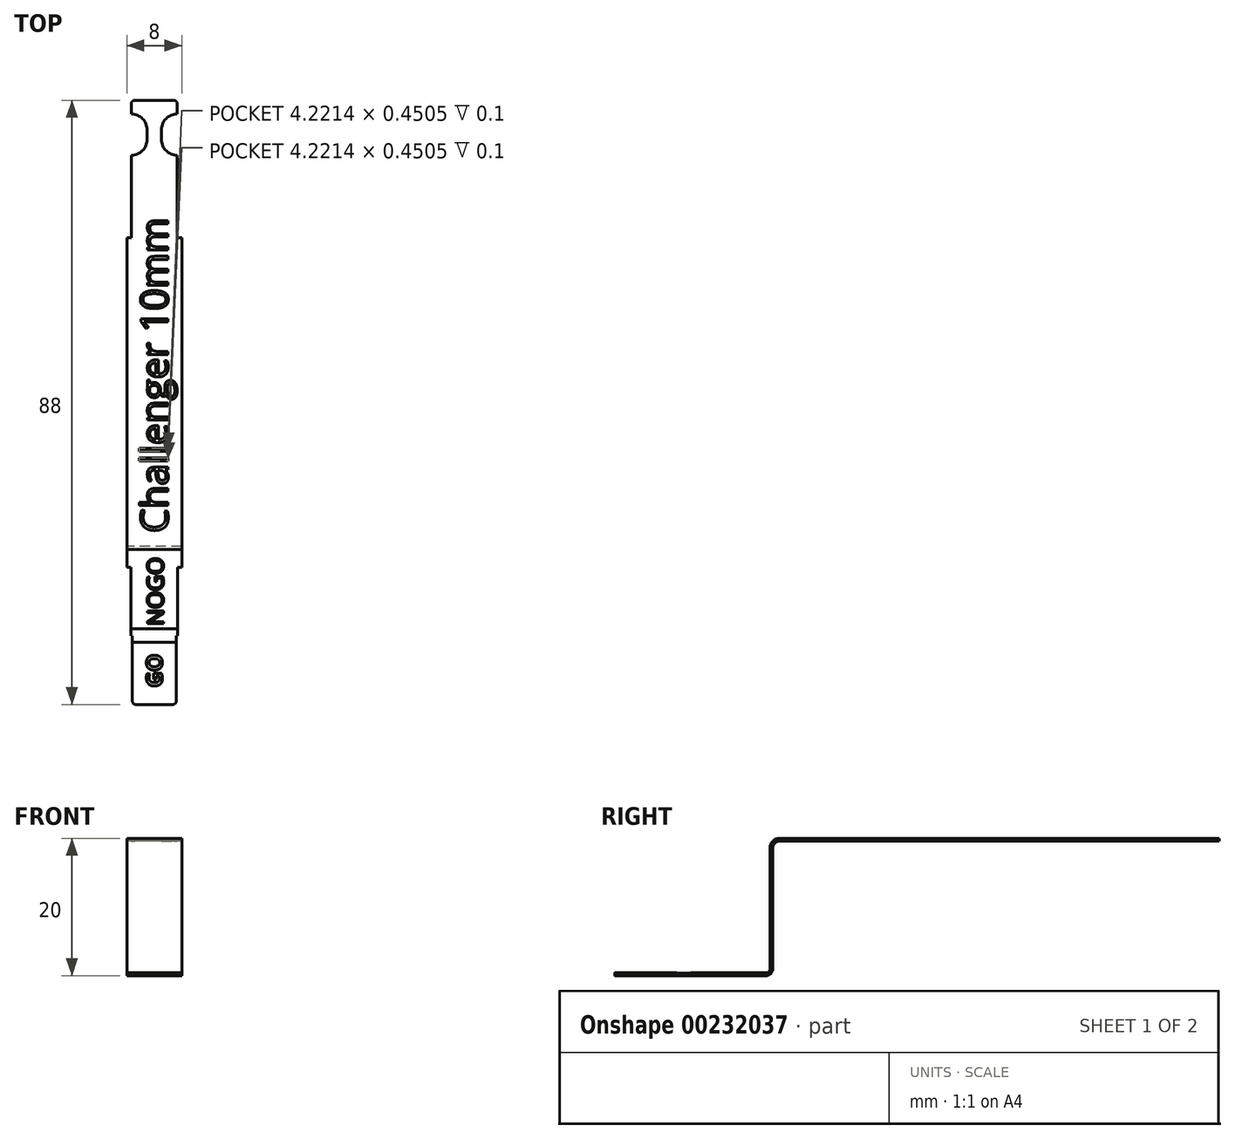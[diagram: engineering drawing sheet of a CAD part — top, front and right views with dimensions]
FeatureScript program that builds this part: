
annotation { "Feature Type Name" : "Feature", "Feature Type Description" : "" }
export const myFeature = defineFeature(function(context is Context, id is Id, definition is map)
    precondition{}
    {
        {
            var Q0;
            Q0=qCreatedBy(makeId("Front.planeOp"),FACE);
            var sketch = newSketch(context, id + "F0", { "sketchPlane" : qUnion([Q0])});
            skLineSegment(sketch, "E0.bottom", {"start": v(-3.2, 0) * mm, "end": v(3.2, 0) * mm});
            skLineSegment(sketch, "E0.top", {"start": v(-3.2, 0.4) * mm, "end": v(3.2, 0.4) * mm});
            skLineSegment(sketch, "E0.left", {"start": v(-3.2, 0) * mm, "end": v(-3.2, 0.4) * mm});
            skLineSegment(sketch, "E0.right", {"start": v(3.2, 0) * mm, "end": v(3.2, 0.4) * mm});
            skSolve(sketch);
        }
        {
            var Q0;
            Q0=qCreatedBy(makeId("Right.planeOp"),FACE);
            var sketch = newSketch(context, id + "F1", { "sketchPlane" : qUnion([Q0])});
            skLineSegment(sketch, "E1", {"start": v(20, 0) * mm, "end": v(22, 0) * mm});
            skArc(sketch, "E2", {"start": v(22, 0) * mm, "mid": v(22.7, 0.3) * mm, "end": v(23, 1) * mm});
            skLineSegment(sketch, "E3", {"start": v(23, 1) * mm, "end": v(23, 18.6) * mm});
            skArc(sketch, "E4", {"start": v(23, 18.6) * mm, "mid": v(23.3, 19.3) * mm, "end": v(24, 19.6) * mm});
            skLineSegment(sketch, "E5", {"start": v(24, 19.6) * mm, "end": v(68, 19.6) * mm});
            skSolve(sketch);
        }
        {
            var Q0;
            Q0=qCreatedBy(makeId("Right.planeOp"),FACE);
            var sketch = newSketch(context, id + "F2", { "sketchPlane" : qUnion([Q0])});
            skLineSegment(sketch, "E6", {"start": v(0, 0) * mm, "end": v(10, 0) * mm});
            skSolve(sketch);
        }
        {
            var Q0;
            Q0=makeQuery(id+"F0.imprint","IMPRINT",FACE,{"disambiguationData":[TD([[makeQuery(id+"F0.imprint","IMPRINT",EDGE,{"derivedFrom":sQuery(id+"F0.wireOp",EDGE,"E0.bottom")}),1.0]])]});
            var Q1;
            Q1=sQuery(id+"F2.wireOp",EDGE,"E6");
            sweep(context, id + "F3", {"profiles" : qUnion([Q0]), "path" : qUnion([Q1])});
        }
        {
            var Q0;
            Q0=makeQuery(id+"F3.opSweep","CAP_FACE",FACE,{"disambiguationData":[OSD([sQuery(id+"F0.wireOp",EDGE,"E0.bottom"),sQuery(id+"F0.wireOp",EDGE,"E0.top"),sQuery(id+"F0.wireOp",EDGE,"E0.left"),sQuery(id+"F0.wireOp",EDGE,"E0.right"),sQuery(id+"F2.wireOp",VERTEX,"E6.end")])],"isStart":false});
            var sketch = newSketch(context, id + "F4", { "sketchPlane" : qUnion([Q0])});
            skLineSegment(sketch, "E7.bottom", {"start": v(-3.4, 0) * mm, "end": v(3.4, 0) * mm});
            skLineSegment(sketch, "E7.top", {"start": v(-3.4, 0.4) * mm, "end": v(3.4, 0.4) * mm});
            skLineSegment(sketch, "E7.left", {"start": v(-3.4, 0) * mm, "end": v(-3.4, 0.4) * mm});
            skLineSegment(sketch, "E7.right", {"start": v(3.4, 0) * mm, "end": v(3.4, 0.4) * mm});
            skSolve(sketch);
        }
        {
            var Q0;
            Q0=qCreatedBy(makeId("Right.planeOp"),FACE);
            var sketch = newSketch(context, id + "F5", { "sketchPlane" : qUnion([Q0])});
            skLineSegment(sketch, "E8", {"start": v(10, 0) * mm, "end": v(20, 0) * mm});
            skSolve(sketch);
        }
        {
            var Q0;
            {var subQ2=sQuery(id+"F4.wireOp",EDGE,"E7.left");Q0=makeQuery(id+"F4.imprint","IMPRINT",FACE,{"disambiguationData":[TD([[makeQuery(id+"F4.imprint","IMPRINT",EDGE,{"derivedFrom":subQ2}),-1.0]])]});}
            var Q1;
            {var subQ1=sQuery(id+"F2.wireOp",VERTEX,"E6.end");var subQ2=makeQuery(id+"F3.opSweep","CAP_EDGE",EDGE,{"disambiguationData":[OSD([sQuery(id+"F0.wireOp",EDGE,"E0.left"),subQ1])],"isStart":false});Q1=makeQuery(id+"F4.imprint","IMPRINT",FACE,{"disambiguationData":[TD([[makeQuery(id+"F4.imprint","IMPRINT",EDGE,{"derivedFrom":subQ2}),1.0]])]});}
            var Q2;
            {var subQ2=sQuery(id+"F4.wireOp",EDGE,"E7.right");Q2=makeQuery(id+"F4.imprint","IMPRINT",FACE,{"disambiguationData":[TD([[makeQuery(id+"F4.imprint","IMPRINT",EDGE,{"derivedFrom":subQ2}),1.0]])]});}
            var Q3;
            Q3=sQuery(id+"F5.wireOp",EDGE,"E8");
            sweep(context, id + "F6", {"operationType" : NewBodyOperationType.ADD, "profiles" : qUnion([Q0, Q1, Q2]), "path" : qUnion([Q3])});
        }
        {
            var Q0;
            Q0=makeQuery(id+"F6.opSweep","CAP_FACE",FACE,{"disambiguationData":[OSD([sQuery(id+"F4.wireOp",EDGE,"E7.bottom"),sQuery(id+"F4.wireOp",EDGE,"E7.top"),sQuery(id+"F4.wireOp",EDGE,"E7.left"),sQuery(id+"F4.wireOp",EDGE,"E7.right"),sQuery(id+"F5.wireOp",VERTEX,"E8.end")])],"isStart":false});
            var sketch = newSketch(context, id + "F7", { "sketchPlane" : qUnion([Q0])});
            skLineSegment(sketch, "E9.bottom", {"start": v(-4, 0) * mm, "end": v(4, 0) * mm});
            skLineSegment(sketch, "E9.top", {"start": v(-4, 0.4) * mm, "end": v(4, 0.4) * mm});
            skLineSegment(sketch, "E9.left", {"start": v(-4, 0) * mm, "end": v(-4, 0.4) * mm});
            skLineSegment(sketch, "E9.right", {"start": v(4, 0) * mm, "end": v(4, 0.4) * mm});
            skSolve(sketch);
        }
        {
            var Q0;
            {var subQ2=sQuery(id+"F7.wireOp",EDGE,"E9.left");Q0=makeQuery(id+"F7.imprint","IMPRINT",FACE,{"disambiguationData":[TD([[makeQuery(id+"F7.imprint","IMPRINT",EDGE,{"derivedFrom":subQ2}),-1.0]])]});}
            var Q1;
            {var subQ1=sQuery(id+"F5.wireOp",VERTEX,"E8.end");var subQ2=makeQuery(id+"F6.opSweep","CAP_EDGE",EDGE,{"disambiguationData":[OSD([sQuery(id+"F4.wireOp",EDGE,"E7.left"),subQ1])],"isStart":false});Q1=makeQuery(id+"F7.imprint","IMPRINT",FACE,{"disambiguationData":[TD([[makeQuery(id+"F7.imprint","IMPRINT",EDGE,{"derivedFrom":subQ2}),1.0]])]});}
            var Q2;
            {var subQ2=sQuery(id+"F7.wireOp",EDGE,"E9.right");Q2=makeQuery(id+"F7.imprint","IMPRINT",FACE,{"disambiguationData":[TD([[makeQuery(id+"F7.imprint","IMPRINT",EDGE,{"derivedFrom":subQ2}),1.0]])]});}
            var Q3;
            Q3=sQuery(id+"F1.wireOp",EDGE,"E1");
            var Q4;
            Q4=sQuery(id+"F1.wireOp",EDGE,"E2");
            var Q5;
            Q5=sQuery(id+"F1.wireOp",EDGE,"E3");
            var Q6;
            Q6=sQuery(id+"F1.wireOp",EDGE,"E4");
            var Q7;
            Q7=sQuery(id+"F1.wireOp",EDGE,"E5");
            var Q8;
            Q8=sQuery(id+"F1.wireOp",EDGE,"802f51ac-a6b9-4bc9-a6be-643a2ca0bfef");
            var Q9;
            Q9=sQuery(id+"F1.wireOp",EDGE,"bahqX9j6-WgO0-pjV7-Zp4m-g6kU4WoMYubH");
            var Q10;
            Q10=sQuery(id+"F1.wireOp",EDGE,"8128329d-e7e9-4f82-aab5-0fca328c60ec");
            var Q11;
            Q11=sQuery(id+"F1.wireOp",EDGE,"NXYmhxNI-pmp3-mEEK-LLts-Cz3JYrwu0ula");
            sweep(context, id + "F8", {"operationType" : NewBodyOperationType.ADD, "profiles" : qUnion([Q0, Q1, Q2]), "path" : qUnion([Q3, Q4, Q5, Q6, Q7, Q8, Q9, Q10, Q11])});
        }
        {
            var Q0;
            Q0=makeQuery(id+"F8.opSweep","CAP_FACE",FACE,{"disambiguationData":[OSD([sQuery(id+"F1.wireOp",VERTEX,"NXYmhxNI-pmp3-mEEK-LLts-Cz3JYrwu0ula.end"),sQuery(id+"F7.wireOp",EDGE,"E9.bottom"),sQuery(id+"F7.wireOp",EDGE,"E9.top"),sQuery(id+"F7.wireOp",EDGE,"E9.left"),sQuery(id+"F7.wireOp",EDGE,"E9.right")])],"isStart":false});
            var sketch = newSketch(context, id + "F9", { "sketchPlane" : qUnion([Q0])});
            skLineSegment(sketch, "E10.bottom", {"start": v(-3.35, 19.6) * mm, "end": v(3.35, 19.6) * mm});
            skLineSegment(sketch, "E10.top", {"start": v(-3.35, 20) * mm, "end": v(3.35, 20) * mm});
            skLineSegment(sketch, "E10.left", {"start": v(-3.35, 19.6) * mm, "end": v(-3.35, 20) * mm});
            skLineSegment(sketch, "E10.right", {"start": v(3.35, 19.6) * mm, "end": v(3.35, 20) * mm});
            skSolve(sketch);
        }
        {
            var Q0;
            Q0=qCreatedBy(makeId("Right.planeOp"),FACE);
            var sketch = newSketch(context, id + "F10", { "sketchPlane" : qUnion([Q0])});
            skLineSegment(sketch, "E11", {"start": v(68, 19.6) * mm, "end": v(88, 19.6) * mm});
            skSolve(sketch);
        }
        {
            var Q0;
            Q0=makeQuery(id+"F9.imprint","IMPRINT",FACE,{"disambiguationData":[TD([[makeQuery(id+"F9.imprint","IMPRINT",EDGE,{"derivedFrom":sQuery(id+"F9.wireOp",EDGE,"E10.bottom")}),1.0]])]});
            var Q1;
            Q1=sQuery(id+"F10.wireOp",EDGE,"E11");
            sweep(context, id + "F11", {"operationType" : NewBodyOperationType.ADD, "profiles" : qUnion([Q0]), "path" : qUnion([Q1])});
        }
        {
            var Q0;
            Q0=makeQuery(id+"F11.opSweep","CAP_EDGE",EDGE,{"disambiguationData":[OSD([sQuery(id+"F9.wireOp",EDGE,"E10.left"),sQuery(id+"F10.wireOp",VERTEX,"E11.end")])],"isStart":false});
            var Q1;
            Q1=makeQuery(id+"F11.opSweep","CAP_EDGE",EDGE,{"disambiguationData":[OSD([sQuery(id+"F9.wireOp",EDGE,"E10.right"),sQuery(id+"F10.wireOp",VERTEX,"E11.end")])],"isStart":false});
            var Q2;
            Q2=makeQuery(id+"F3.opSweep","CAP_EDGE",EDGE,{"disambiguationData":[OSD([sQuery(id+"F0.wireOp",EDGE,"E0.right"),sQuery(id+"F2.wireOp",VERTEX,"E6.start")])],"isStart":true});
            var Q3;
            Q3=makeQuery(id+"F3.opSweep","CAP_EDGE",EDGE,{"disambiguationData":[OSD([sQuery(id+"F0.wireOp",EDGE,"E0.left"),sQuery(id+"F2.wireOp",VERTEX,"E6.start")])],"isStart":true});
            fillet(context, id + "F12", {"entities" : qUnion([Q0, Q1, Q2, Q3]), "radius" : 0.5 * mm, "tangentPropagation" : true, "allowEdgeOverflow" : false});
        }
        {
            var Q0;
            Q0=makeQuery(id+"F8.boolean.opBoolean","MERGE",FACE,{"derivedFrom":[makeQuery(id+"F6.boolean.opBoolean","MERGE",FACE,{"derivedFrom":[makeQuery(id+"F3.opSweep","SWEPT_FACE",FACE,{"disambiguationData":[OSD([sQuery(id+"F0.wireOp",EDGE,"E0.top"),sQuery(id+"F2.wireOp",EDGE,"E6")])]}),makeQuery(id+"F6.opSweep","SWEPT_FACE",FACE,{"disambiguationData":[OSD([sQuery(id+"F4.wireOp",EDGE,"E7.top"),sQuery(id+"F5.wireOp",EDGE,"E8")])]})]}),makeQuery(id+"F8.opSweep","SWEPT_FACE",FACE,{"disambiguationData":[OSD([sQuery(id+"F1.wireOp",EDGE,"E1"),sQuery(id+"F7.wireOp",EDGE,"E9.top")])]})]});
            var sketch = newSketch(context, id + "F13", { "sketchPlane" : qUnion([Q0])});
            skText(sketch, "E12", { "text": "GO", "fontName": "OpenSans-Bold.ttf"});
            const initialGuessF13  = {"E12": [0.00115, 0.0025, 0, 1, 0.0023]};
            skSetInitialGuess(sketch, initialGuessF13);
            skSolve(sketch);
        }
        {
            var Q0;
            Q0=makeQuery(id+"F13.imprint","IMPRINT",FACE,{"disambiguationData":[TD([[makeQuery(id+"F13.imprint","IMPRINT",EDGE,{"derivedFrom":sQuery(id+"F13.wireOp",EDGE,"E12.sketch_text.stroke-0")}),-1.0]])]});
            var Q1;
            Q1=makeQuery(id+"F13.imprint","IMPRINT",FACE,{"disambiguationData":[TD([[makeQuery(id+"F13.imprint","IMPRINT",EDGE,{"derivedFrom":sQuery(id+"F13.wireOp",EDGE,"E12.sketch_text.stroke-19")}),-1.0]])]});
            extrude(context, id + "F14", {"entities" : qUnion([Q0, Q1]), "operationType" : NewBodyOperationType.REMOVE, "oppositeDirection" : true, "depth" : 0.05 * mm});
        }
        {
            var Q0;
            {var subQ2=sQuery(id+"F4.wireOp",EDGE,"E7.top");var subQ7=sQuery(id+"F1.wireOp",EDGE,"E1");var subQ8=sQuery(id+"F2.wireOp",EDGE,"E6");var subQ9=sQuery(id+"F0.wireOp",EDGE,"E0.top");var subQ10=sQuery(id+"F5.wireOp",EDGE,"E8");var subQ12=sQuery(id+"F7.wireOp",EDGE,"E9.top");Q0=makeQuery(id+"F14.boolean.opBoolean","SPLIT",FACE,{"disambiguationData":[TD([makeQuery(id+"F14.opExtrude","SWEPT_FACE",FACE,{"disambiguationData":[OSD([sQuery(id+"F13.wireOp",EDGE,"E12.sketch_text.stroke-0")])]})])],"derivedFrom":makeQuery(id+"F8.boolean.opBoolean","MERGE",FACE,{"derivedFrom":[makeQuery(id+"F6.boolean.opBoolean","MERGE",FACE,{"derivedFrom":[makeQuery(id+"F3.opSweep","SWEPT_FACE",FACE,{"disambiguationData":[OSD([subQ9,subQ8])]}),makeQuery(id+"F6.opSweep","SWEPT_FACE",FACE,{"disambiguationData":[OSD([subQ2,subQ10])]})]}),makeQuery(id+"F8.opSweep","SWEPT_FACE",FACE,{"disambiguationData":[OSD([subQ7,subQ12])]})]})});}
            var sketch = newSketch(context, id + "F15", { "sketchPlane" : qUnion([Q0])});
            skLineSegment(sketch, "E13.bottom", {"start": v(-3.4, 9.04) * mm, "end": v(3.4, 9.04) * mm});
            skLineSegment(sketch, "E13.top", {"start": v(-3.4, 11.04) * mm, "end": v(3.4, 11.04) * mm});
            skLineSegment(sketch, "E13.left", {"start": v(-3.4, 9.04) * mm, "end": v(-3.4, 11.04) * mm});
            skLineSegment(sketch, "E13.right", {"start": v(3.4, 9.04) * mm, "end": v(3.4, 11.04) * mm});
            skSolve(sketch);
        }
        {
            var Q0;
            Q0=makeQuery(id+"F15.imprint","IMPRINT",FACE,{"disambiguationData":[TD([[makeQuery(id+"F15.imprint","IMPRINT",EDGE,{"derivedFrom":sQuery(id+"F15.wireOp",EDGE,"E13.top")}),-1.0]])]});
            extrude(context, id + "F16", {"entities" : qUnion([Q0]), "operationType" : NewBodyOperationType.REMOVE, "oppositeDirection" : true, "depth" : 0.05 * mm});
        }
        {
            var Q0;
            Q0=makeQuery(id+"F11.boolean.opBoolean","MERGE",FACE,{"derivedFrom":[makeQuery(id+"F8.opSweep","SWEPT_FACE",FACE,{"disambiguationData":[OSD([sQuery(id+"F1.wireOp",EDGE,"E5"),sQuery(id+"F7.wireOp",EDGE,"E9.top")])]}),makeQuery(id+"F11.opSweep","SWEPT_FACE",FACE,{"disambiguationData":[OSD([sQuery(id+"F9.wireOp",EDGE,"E10.top"),sQuery(id+"F10.wireOp",EDGE,"E11")])]})]});
            var sketch = newSketch(context, id + "F17", { "sketchPlane" : qUnion([Q0])});
            skLineSegment(sketch, "E14", {"start": v(1.05, 82.3) * mm, "end": v(1.05, 83.7) * mm});
            skArc(sketch, "E15", {"start": v(1.05, 83.7) * mm, "mid": v(1.72, 85.33) * mm, "end": v(3.35, 86) * mm});
            skArc(sketch, "E16", {"start": v(1.05, 82.3) * mm, "mid": v(1.72, 80.67) * mm, "end": v(3.35, 80) * mm});
            skLineSegment(sketch, "E17", {"start": v(0, 78.21) * mm, "end": v(0, 88) * mm, "construction": true});
            skLineSegment(sketch, "E18.MirrorCS", {"start": v(-1.05, 82.3) * mm, "end": v(-1.05, 83.7) * mm});
            skArc(sketch, "E19.MirrorCS", {"start": v(-1.05, 83.7) * mm, "mid": v(-1.72, 85.33) * mm, "end": v(-3.35, 86) * mm});
            skArc(sketch, "E20.MirrorCS", {"start": v(-1.05, 82.3) * mm, "mid": v(-1.72, 80.67) * mm, "end": v(-3.35, 80) * mm});
            skSolve(sketch);
        }
        {
            var Q0;
            Q0=makeQuery(id+"F17.imprint","IMPRINT",FACE,{"disambiguationData":[TD([[makeQuery(id+"F17.imprint","IMPRINT",EDGE,{"derivedFrom":sQuery(id+"F17.wireOp",EDGE,"E14")}),-1.0]])]});
            var Q1;
            Q1=makeQuery(id+"F17.imprint","IMPRINT",FACE,{"disambiguationData":[TD([[makeQuery(id+"F17.imprint","IMPRINT",EDGE,{"derivedFrom":sQuery(id+"F17.wireOp",EDGE,"E18.MirrorCS")}),1.0]])]});
            extrude(context, id + "F18", {"entities" : qUnion([Q0, Q1]), "operationType" : NewBodyOperationType.REMOVE, "endBound" : BoundingType.THROUGH_ALL, "oppositeDirection" : true, "depth" : 25 * mm});
        }
        {
            var Q0;
            {var subQ2=sQuery(id+"F7.wireOp",EDGE,"E9.top");var subQ4=sQuery(id+"F1.wireOp",EDGE,"E1");var subQ6=sQuery(id+"F5.wireOp",EDGE,"E8");var subQ16=sQuery(id+"F0.wireOp",EDGE,"E0.top");var subQ17=sQuery(id+"F4.wireOp",EDGE,"E7.top");var subQ18=sQuery(id+"F2.wireOp",EDGE,"E6");Q0=makeQuery(id+"F16.boolean.opBoolean","SPLIT",FACE,{"disambiguationData":[TD([makeQuery(id+"F16.opExtrude","SWEPT_FACE",FACE,{"disambiguationData":[OSD([sQuery(id+"F15.wireOp",EDGE,"E13.top")])]})])],"derivedFrom":makeQuery(id+"F14.boolean.opBoolean","SPLIT",FACE,{"disambiguationData":[TD([makeQuery(id+"F14.opExtrude","SWEPT_FACE",FACE,{"disambiguationData":[OSD([sQuery(id+"F13.wireOp",EDGE,"E12.sketch_text.stroke-0")])]})])],"derivedFrom":makeQuery(id+"F8.boolean.opBoolean","MERGE",FACE,{"derivedFrom":[makeQuery(id+"F6.boolean.opBoolean","MERGE",FACE,{"derivedFrom":[makeQuery(id+"F3.opSweep","SWEPT_FACE",FACE,{"disambiguationData":[OSD([subQ16,subQ18])]}),makeQuery(id+"F6.opSweep","SWEPT_FACE",FACE,{"disambiguationData":[OSD([subQ17,subQ6])]})]}),makeQuery(id+"F8.opSweep","SWEPT_FACE",FACE,{"disambiguationData":[OSD([subQ4,subQ2])]})]})})});}
            var sketch = newSketch(context, id + "F19", { "sketchPlane" : qUnion([Q0])});
            skText(sketch, "E21", { "text": "NOGO\n", "fontName": "OpenSans-Regular.ttf"});
            const initialGuessF19  = {"E21": [0.00133, 0.01145, 0, 1, 0.00237]};
            skSetInitialGuess(sketch, initialGuessF19);
            skSolve(sketch);
        }
        {
            var Q0;
            Q0 = qSketchRegion(id + "F19", true);
            extrude(context, id + "F20", {"entities" : qUnion([Q0]), "operationType" : NewBodyOperationType.REMOVE, "oppositeDirection" : true, "depth" : 0.1 * mm});
        }
        {
            var Q0;
            Q0=makeQuery(id+"F11.boolean.opBoolean","MERGE",FACE,{"derivedFrom":[makeQuery(id+"F8.opSweep","SWEPT_FACE",FACE,{"disambiguationData":[OSD([sQuery(id+"F1.wireOp",EDGE,"E5"),sQuery(id+"F7.wireOp",EDGE,"E9.top")])]}),makeQuery(id+"F11.opSweep","SWEPT_FACE",FACE,{"disambiguationData":[OSD([sQuery(id+"F9.wireOp",EDGE,"E10.top"),sQuery(id+"F10.wireOp",EDGE,"E11")])]})]});
            var sketch = newSketch(context, id + "F21", { "sketchPlane" : qUnion([Q0])});
            skText(sketch, "E22", { "text": "Challenger 10mm", "fontName": "OpenSans-Regular.ttf"});
            const initialGuessF21  = {"E22": [0.002, 0.025, 0, 1, 0.004]};
            skSetInitialGuess(sketch, initialGuessF21);
            skSolve(sketch);
        }
        {
            var Q0;
            Q0=makeQuery(id+"F21.imprint","IMPRINT",FACE,{"disambiguationData":[TD([[makeQuery(id+"F21.imprint","IMPRINT",EDGE,{"derivedFrom":sQuery(id+"F21.wireOp",EDGE,"E22.sketch_text.stroke-0")}),-1.0]])]});
            var Q1;
            Q1=makeQuery(id+"F21.imprint","IMPRINT",FACE,{"disambiguationData":[TD([[makeQuery(id+"F21.imprint","IMPRINT",EDGE,{"derivedFrom":sQuery(id+"F21.wireOp",EDGE,"E22.sketch_text.stroke-15")}),-1.0]])]});
            var Q2;
            Q2=makeQuery(id+"F21.imprint","IMPRINT",FACE,{"disambiguationData":[TD([[makeQuery(id+"F21.imprint","IMPRINT",EDGE,{"derivedFrom":sQuery(id+"F21.wireOp",EDGE,"E22.sketch_text.stroke-33")}),-1.0]])]});
            var Q3;
            Q3=makeQuery(id+"F21.imprint","IMPRINT",FACE,{"disambiguationData":[TD([[makeQuery(id+"F21.imprint","IMPRINT",EDGE,{"derivedFrom":sQuery(id+"F21.wireOp",EDGE,"E22.sketch_text.stroke-60")}),-1.0]])]});
            var Q4;
            Q4=makeQuery(id+"F21.imprint","IMPRINT",FACE,{"disambiguationData":[TD([[makeQuery(id+"F21.imprint","IMPRINT",EDGE,{"derivedFrom":sQuery(id+"F21.wireOp",EDGE,"E22.sketch_text.stroke-64")}),-1.0]])]});
            var Q5;
            Q5=makeQuery(id+"F21.imprint","IMPRINT",FACE,{"disambiguationData":[TD([[makeQuery(id+"F21.imprint","IMPRINT",EDGE,{"derivedFrom":sQuery(id+"F21.wireOp",EDGE,"E22.sketch_text.stroke-68")}),-1.0]])]});
            var Q6;
            Q6=makeQuery(id+"F21.imprint","IMPRINT",FACE,{"disambiguationData":[TD([[makeQuery(id+"F21.imprint","IMPRINT",EDGE,{"derivedFrom":sQuery(id+"F21.wireOp",EDGE,"E22.sketch_text.stroke-87")}),-1.0]])]});
            var Q7;
            Q7=makeQuery(id+"F21.imprint","IMPRINT",FACE,{"disambiguationData":[TD([[makeQuery(id+"F21.imprint","IMPRINT",EDGE,{"derivedFrom":sQuery(id+"F21.wireOp",EDGE,"E22.sketch_text.stroke-104")}),-1.0]])]});
            var Q8;
            Q8=makeQuery(id+"F21.imprint","IMPRINT",FACE,{"disambiguationData":[TD([[makeQuery(id+"F21.imprint","IMPRINT",EDGE,{"derivedFrom":sQuery(id+"F21.wireOp",EDGE,"E22.sketch_text.stroke-148")}),-1.0]])]});
            var Q9;
            Q9=makeQuery(id+"F21.imprint","IMPRINT",FACE,{"disambiguationData":[TD([[makeQuery(id+"F21.imprint","IMPRINT",EDGE,{"derivedFrom":sQuery(id+"F21.wireOp",EDGE,"E22.sketch_text.stroke-167")}),-1.0]])]});
            var Q10;
            Q10=makeQuery(id+"F21.imprint","IMPRINT",FACE,{"disambiguationData":[TD([[makeQuery(id+"F21.imprint","IMPRINT",EDGE,{"derivedFrom":sQuery(id+"F21.wireOp",EDGE,"E22.sketch_text.stroke-180")}),-1.0]])]});
            var Q11;
            Q11=makeQuery(id+"F21.imprint","IMPRINT",FACE,{"disambiguationData":[TD([[makeQuery(id+"F21.imprint","IMPRINT",EDGE,{"derivedFrom":sQuery(id+"F21.wireOp",EDGE,"E22.sketch_text.stroke-189")}),-1.0]])]});
            var Q12;
            Q12=makeQuery(id+"F21.imprint","IMPRINT",FACE,{"disambiguationData":[TD([[makeQuery(id+"F21.imprint","IMPRINT",EDGE,{"derivedFrom":sQuery(id+"F21.wireOp",EDGE,"E22.sketch_text.stroke-205")}),-1.0]])]});
            var Q13;
            Q13=makeQuery(id+"F21.imprint","IMPRINT",FACE,{"disambiguationData":[TD([[makeQuery(id+"F21.imprint","IMPRINT",EDGE,{"derivedFrom":sQuery(id+"F21.wireOp",EDGE,"E22.sketch_text.stroke-233")}),-1.0]])]});
            extrude(context, id + "F22", {"entities" : qUnion([Q0, Q1, Q2, Q3, Q4, Q5, Q6, Q7, Q8, Q9, Q10, Q11, Q12, Q13]), "operationType" : NewBodyOperationType.REMOVE, "oppositeDirection" : true, "depth" : 0.1 * mm});
        }
    });
